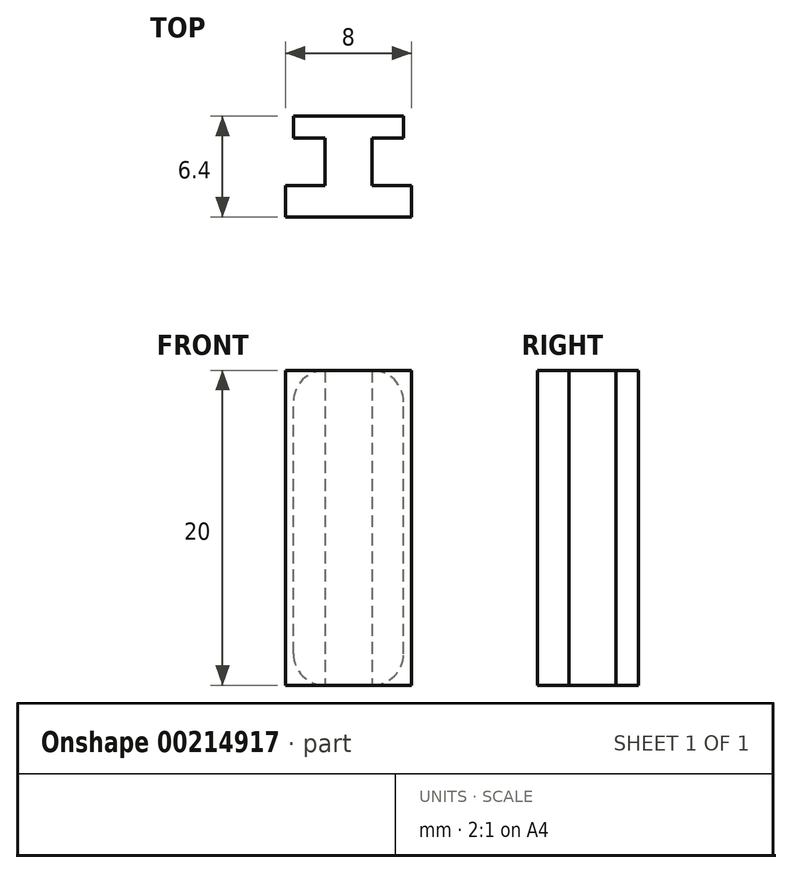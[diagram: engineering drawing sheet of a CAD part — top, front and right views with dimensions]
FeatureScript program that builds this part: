
annotation { "Feature Type Name" : "Feature", "Feature Type Description" : "" }
export const myFeature = defineFeature(function(context is Context, id is Id, definition is map)
    precondition{}
    {
        {
            var Q0;
            Q0=qCreatedBy(makeId("Front.planeOp"),FACE);
            var sketch = newSketch(context, id + "F0", { "sketchPlane" : qUnion([Q0])});
            skLineSegment(sketch, "E0.bottom", {"start": v(3.5, -10) * mm, "end": v(-3.5, -10) * mm});
            skLineSegment(sketch, "E0.top", {"start": v(3.5, 10) * mm, "end": v(-3.5, 10) * mm});
            skLineSegment(sketch, "E0.left", {"start": v(3.5, -10) * mm, "end": v(3.5, 10) * mm});
            skLineSegment(sketch, "E0.right", {"start": v(-3.5, -10) * mm, "end": v(-3.5, 10) * mm});
            skPoint(sketch, "E0.middle", {"position": v(0, 0) * mm});
            skSolve(sketch);
        }
        {
            var Q0;
            Q0=makeQuery(id+"F0.imprint","IMPRINT",FACE,{"disambiguationData":[TD([[makeQuery(id+"F0.imprint","IMPRINT",EDGE,{"derivedFrom":sQuery(id+"F0.wireOp",EDGE,"E0.bottom")}),-1.0]])]});
            extrude(context, id + "F1", {"entities" : qUnion([Q0]), "depth" : 1.4 * mm});
        }
        {
            var Q0;
            Q0=makeQuery(id+"F1.opExtrude","CAP_FACE",FACE,{"disambiguationData":[OSD([sQuery(id+"F0.wireOp",EDGE,"E0.bottom"),sQuery(id+"F0.wireOp",EDGE,"E0.top"),sQuery(id+"F0.wireOp",EDGE,"E0.left"),sQuery(id+"F0.wireOp",EDGE,"E0.right")])],"isStart":false});
            var sketch = newSketch(context, id + "F2", { "sketchPlane" : qUnion([Q0])});
            skLineSegment(sketch, "E1.bottom", {"start": v(1.5, 10) * mm, "end": v(-1.5, 10) * mm});
            skLineSegment(sketch, "E1.top", {"start": v(1.5, -10) * mm, "end": v(-1.5, -10) * mm});
            skLineSegment(sketch, "E1.left", {"start": v(1.5, 10) * mm, "end": v(1.5, -10) * mm});
            skLineSegment(sketch, "E1.right", {"start": v(-1.5, 10) * mm, "end": v(-1.5, -10) * mm});
            skPoint(sketch, "E1.middle", {"position": v(0, 0) * mm});
            skSolve(sketch);
        }
        {
            var Q0;
            Q0=makeQuery(id+"F2.imprint","IMPRINT",FACE,{"disambiguationData":[TD([[makeQuery(id+"F2.imprint","IMPRINT",EDGE,{"derivedFrom":sQuery(id+"F2.wireOp",EDGE,"E1.bottom")}),1.0]])]});
            extrude(context, id + "F3", {"entities" : qUnion([Q0]), "operationType" : NewBodyOperationType.ADD, "depth" : 3 * mm});
        }
        {
            var Q0;
            Q0=makeQuery(id+"F3.opExtrude","CAP_FACE",FACE,{"disambiguationData":[OSD([sQuery(id+"F2.wireOp",EDGE,"E1.bottom"),sQuery(id+"F2.wireOp",EDGE,"E1.top"),sQuery(id+"F2.wireOp",EDGE,"E1.left"),sQuery(id+"F2.wireOp",EDGE,"E1.right")])],"isStart":false});
            var sketch = newSketch(context, id + "F4", { "sketchPlane" : qUnion([Q0])});
            skLineSegment(sketch, "E2.bottom", {"start": v(4, 10) * mm, "end": v(-4, 10) * mm});
            skLineSegment(sketch, "E2.top", {"start": v(4, -10) * mm, "end": v(-4, -10) * mm});
            skLineSegment(sketch, "E2.left", {"start": v(4, 10) * mm, "end": v(4, -10) * mm});
            skLineSegment(sketch, "E2.right", {"start": v(-4, 10) * mm, "end": v(-4, -10) * mm});
            skPoint(sketch, "E2.middle", {"position": v(0, 0) * mm});
            skSolve(sketch);
        }
        {
            var Q0;
            Q0=qSketchRegion(id+"F4",true);
            extrude(context, id + "F5", {"entities" : qUnion([Q0]), "operationType" : NewBodyOperationType.ADD, "depth" : 2 * mm});
        }
        {
            var Q0;
            Q0=makeQuery(id+"F1.opExtrude","SWEPT_EDGE",EDGE,{"disambiguationData":[OSD([sQuery(id+"F0.wireOp",EDGE,"E0.top"),sQuery(id+"F0.wireOp",EDGE,"E0.left")])]});
            var Q1;
            Q1=makeQuery(id+"F1.opExtrude","SWEPT_EDGE",EDGE,{"disambiguationData":[OSD([sQuery(id+"F0.wireOp",EDGE,"E0.top"),sQuery(id+"F0.wireOp",EDGE,"E0.right")])]});
            var Q2;
            Q2=makeQuery(id+"F1.opExtrude","SWEPT_EDGE",EDGE,{"disambiguationData":[OSD([sQuery(id+"F0.wireOp",EDGE,"E0.bottom"),sQuery(id+"F0.wireOp",EDGE,"E0.left")])]});
            var Q3;
            Q3=makeQuery(id+"F1.opExtrude","SWEPT_EDGE",EDGE,{"disambiguationData":[OSD([sQuery(id+"F0.wireOp",EDGE,"E0.bottom"),sQuery(id+"F0.wireOp",EDGE,"E0.right")])]});
            fillet(context, id + "F6", {"entities" : qUnion([Q0, Q1, Q2, Q3]), "radius" : 2 * mm, "tangentPropagation" : true, "allowEdgeOverflow" : false});
        }
    });
